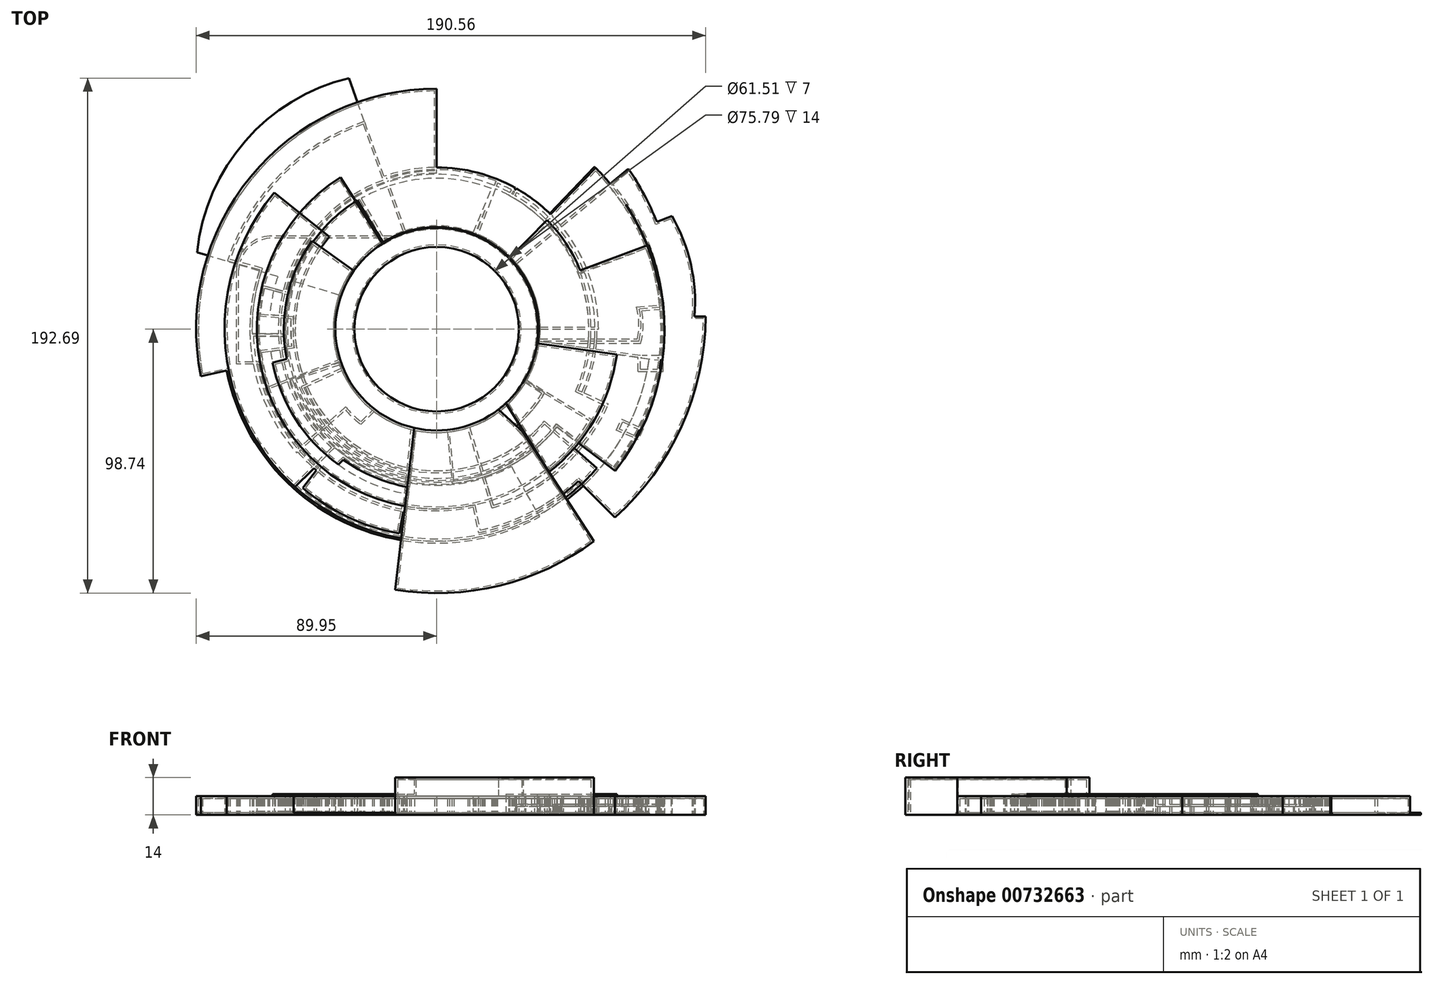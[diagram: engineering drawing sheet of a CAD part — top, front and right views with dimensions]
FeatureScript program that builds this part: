
annotation { "Feature Type Name" : "Feature", "Feature Type Description" : "" }
export const myFeature = defineFeature(function(context is Context, id is Id, definition is map)
    precondition{}
    {
        {
            var Q0;
            Q0=qCreatedBy(makeId("Top.planeOp"),FACE);
            var sketch = newSketch(context, id + "F0", { "sketchPlane" : qUnion([Q0])});
            skCircle(sketch, "E0", {"center": v(0, 0) * mm, "radius": 37.9 * mm});
            skArc(sketch, "E1", {"start": v(-50.12, -59.4) * mm, "mid": v(-33.16, -70.3) * mm, "end": v(-13.98, -76.46) * mm});
            skLineSegment(sketch, "E2", {"start": v(-14.9, 34.84) * mm, "end": v(-60.57, 34.84) * mm});
            skLineSegment(sketch, "E3.bottom", {"start": v(-60.57, 34.84) * mm, "end": v(-14.9, 34.84) * mm});
            skLineSegment(sketch, "E4", {"start": v(28.82, 24.6) * mm, "end": v(71.63, 60.04) * mm});
            skLineSegment(sketch, "E5", {"start": v(-44.15, -51.62) * mm, "end": v(-50.12, -59.4) * mm});
            skLineSegment(sketch, "E6", {"start": v(-66.66, -13.02) * mm, "end": v(-74.87, -13.02) * mm});
            skLineSegment(sketch, "E7", {"start": v(-74.87, -13.02) * mm, "end": v(-74.87, 22.1) * mm});
            skLineSegment(sketch, "E8", {"start": v(-60.57, 34.84) * mm, "end": v(-62.55, 34.84) * mm});
            skArc(sketch, "E9", {"start": v(-60.57, 34.84) * mm, "mid": v(-70.41, 31.5) * mm, "end": v(-74.87, 22.1) * mm});
            skLineSegment(sketch, "E10", {"start": v(53.03, -56.83) * mm, "end": v(66.67, -70.45) * mm});
            skArc(sketch, "E11", {"start": v(66.67, -70.45) * mm, "mid": v(91.53, -36.42) * mm, "end": v(100.6, 4.75) * mm});
            skLineSegment(sketch, "E12", {"start": v(100.6, 4.75) * mm, "end": v(96.37, 4.75) * mm});
            skArc(sketch, "E13", {"start": v(96.37, 4.75) * mm, "mid": v(95.04, 24.16) * mm, "end": v(87.94, 42.28) * mm});
            skLineSegment(sketch, "E14", {"start": v(87.94, 42.28) * mm, "end": v(82.34, 40.14) * mm});
            skArc(sketch, "E15", {"start": v(82.34, 40.14) * mm, "mid": v(77.54, 50.39) * mm, "end": v(71.63, 60.04) * mm});
            skLineSegment(sketch, "E16", {"start": v(-13.98, -76.46) * mm, "end": v(-12.25, -66.8) * mm});
            skLineSegment(sketch, "E17", {"start": v(13.53, -66.56) * mm, "end": v(15.57, -76.15) * mm});
            skArc(sketch, "E18.trimOffspring", {"start": v(15.57, -76.15) * mm, "mid": v(35.63, -69.08) * mm, "end": v(53.03, -56.83) * mm});
            skArc(sketch, "E19.trimOffspring", {"start": v(-12.25, -66.8) * mm, "mid": v(0.65, -67.92) * mm, "end": v(13.53, -66.56) * mm});
            skArc(sketch, "E20.trimOffspring", {"start": v(-66.66, -13.02) * mm, "mid": v(-58.67, -34.22) * mm, "end": v(-44.15, -51.62) * mm});
            skLineSegment(sketch, "E21", {"start": v(68.27, -37.37) * mm, "end": v(69.5, -34.68) * mm});
            skLineSegment(sketch, "E22", {"start": v(69.5, -34.68) * mm, "end": v(76.13, -37.73) * mm});
            skLineSegment(sketch, "E23", {"start": v(76.13, -37.73) * mm, "end": v(74.95, -40.3) * mm});
            skLineSegment(sketch, "E24", {"start": v(74.95, -40.3) * mm, "end": v(68.27, -37.37) * mm});
            skLineSegment(sketch, "E25", {"start": v(76.13, -15) * mm, "end": v(83.94, -15) * mm});
            skLineSegment(sketch, "E26", {"start": v(83.94, -15) * mm, "end": v(83.94, -10.7) * mm});
            skLineSegment(sketch, "E27", {"start": v(83.94, -10.7) * mm, "end": v(76.13, -10.7) * mm});
            skLineSegment(sketch, "E28", {"start": v(76.13, -15) * mm, "end": v(76.13, -10.7) * mm});
            skLineSegment(sketch, "E29", {"start": v(37.63, -4.5) * mm, "end": v(75.65, -4.5) * mm});
            skLineSegment(sketch, "E30", {"start": v(75.7, 7.57) * mm, "end": v(84.16, 8.26) * mm});
            skArc(sketch, "E31", {"start": v(75.65, -4.5) * mm, "mid": v(76.39, 1.54) * mm, "end": v(75.7, 7.57) * mm});
            skArc(sketch, "E32", {"start": v(84.16, 8.26) * mm, "mid": v(78.2, 32.88) * mm, "end": v(64.7, 54.32) * mm});
            skSolve(sketch);
        }
        {
            var Q0;
            {var subQ4=sQuery(id+"F0.wireOp",EDGE,"E29");Q0=makeQuery(id+"F0.imprint","IMPRINT",FACE,{"disambiguationData":[TD([[makeQuery(id+"F0.imprint","IMPRINT",EDGE,{"derivedFrom":subQ4}),1.0]])]});}
            extrude(context, id + "F1", {"entities" : qUnion([Q0]), "depth" : 4 * mm, "offsetDistance" : 25.4 * mm});
        }
        {
            var Q0;
            Q0=makeQuery(id+"F1.opExtrude","CAP_FACE",FACE,{"disambiguationData":[OSD([sQuery(id+"F0.wireOp",EDGE,"E0"),sQuery(id+"F0.wireOp",EDGE,"E4"),sQuery(id+"F0.wireOp",EDGE,"E29"),sQuery(id+"F0.wireOp",EDGE,"E30"),sQuery(id+"F0.wireOp",EDGE,"E31"),sQuery(id+"F0.wireOp",EDGE,"E32")])],"isStart":true});
            shell(context, id + "F2", {"entities" : qUnion([Q0]), "thickness" : 0.8 * mm});
        }
        {
            var Q0;
            Q0=makeQuery(id+"F0.imprint","IMPRINT",FACE,{"disambiguationData":[TD([[makeQuery(id+"F0.imprint","IMPRINT",EDGE,{"derivedFrom":sQuery(id+"F0.wireOp",EDGE,"E1")}),1.0]])]});
            extrude(context, id + "F3", {"entities" : qUnion([Q0]), "operationType" : NewBodyOperationType.ADD, "depth" : 7 * mm, "offsetDistance" : 25.4 * mm});
        }
        {
            var Q0;
            {var subQ0=sQuery(id+"F0.wireOp",EDGE,"E32");var subQ1=sQuery(id+"F0.wireOp",EDGE,"E31");var subQ2=sQuery(id+"F0.wireOp",EDGE,"E30");var subQ3=sQuery(id+"F0.wireOp",EDGE,"E29");var subQ4=sQuery(id+"F0.wireOp",EDGE,"E4");var subQ5=sQuery(id+"F0.wireOp",EDGE,"E0");Q0=makeQuery(id+"F3.boolean.opBoolean","MERGE",FACE,{"derivedFrom":[makeQuery(id+"F1.opExtrude","CAP_FACE",FACE,{"disambiguationData":[OSD([subQ5,subQ4,subQ3,subQ2,subQ1,subQ0])],"isStart":true}),makeQuery(id+"F3.opExtrude","CAP_FACE",FACE,{"disambiguationData":[OSD([subQ5,sQuery(id+"F0.wireOp",EDGE,"E1"),sQuery(id+"F0.wireOp",EDGE,"E3.bottom"),subQ4,sQuery(id+"F0.wireOp",EDGE,"E5"),sQuery(id+"F0.wireOp",EDGE,"E6"),sQuery(id+"F0.wireOp",EDGE,"E7"),sQuery(id+"F0.wireOp",EDGE,"E8"),sQuery(id+"F0.wireOp",EDGE,"E9"),sQuery(id+"F0.wireOp",EDGE,"E10"),sQuery(id+"F0.wireOp",EDGE,"E11"),sQuery(id+"F0.wireOp",EDGE,"E12"),sQuery(id+"F0.wireOp",EDGE,"E13"),sQuery(id+"F0.wireOp",EDGE,"E14"),sQuery(id+"F0.wireOp",EDGE,"E15"),sQuery(id+"F0.wireOp",EDGE,"E16"),sQuery(id+"F0.wireOp",EDGE,"E17"),sQuery(id+"F0.wireOp",EDGE,"E18.trimOffspring"),sQuery(id+"F0.wireOp",EDGE,"E19.trimOffspring"),sQuery(id+"F0.wireOp",EDGE,"E20.trimOffspring"),sQuery(id+"F0.wireOp",EDGE,"E21"),sQuery(id+"F0.wireOp",EDGE,"E22"),sQuery(id+"F0.wireOp",EDGE,"E23"),sQuery(id+"F0.wireOp",EDGE,"E24"),sQuery(id+"F0.wireOp",EDGE,"E25"),sQuery(id+"F0.wireOp",EDGE,"E26"),sQuery(id+"F0.wireOp",EDGE,"E27"),sQuery(id+"F0.wireOp",EDGE,"E28"),subQ3,subQ2,subQ1,subQ0])],"isStart":true})]});}
            shell(context, id + "F4", {"entities" : qUnion([Q0]), "thickness" : 0.8 * mm});
        }
        {
            var Q0;
            Q0=qCreatedBy(makeId("Top.planeOp"),FACE);
            var sketch = newSketch(context, id + "F5", { "sketchPlane" : qUnion([Q0])});
            skArc(sketch, "E33.0", {"start": v(-14.9, 34.84) * mm, "mid": v(-22.7, -30.33) * mm, "end": v(37.63, -4.5) * mm});
            skCircle(sketch, "E34", {"center": v(0, 0) * mm, "radius": 37.9 * mm});
            skCircle(sketch, "E35", {"center": v(0, 0) * mm, "radius": 89.95 * mm});
            skCircle(sketch, "E36", {"center": v(0, 0) * mm, "radius": 80.03 * mm});
            skCircle(sketch, "E37", {"center": v(0, 0) * mm, "radius": 58.4 * mm});
            skLineSegment(sketch, "E38", {"start": v(-88.21, -17.57) * mm, "end": v(-78.51, -15.5) * mm});
            skLineSegment(sketch, "E39", {"start": v(-53.51, -59.5) * mm, "end": v(-38.11, -44.24) * mm});
            skLineSegment(sketch, "E40", {"start": v(27.85, -51.32) * mm, "end": v(17.87, -33.42) * mm});
            skLineSegment(sketch, "E41", {"start": v(17.87, -33.42) * mm, "end": v(38.4, -70.22) * mm});
            skLineSegment(sketch, "E42", {"start": v(0, 37.9) * mm, "end": v(0, 89.95) * mm});
            skSolve(sketch);
        }
        {
            var Q0;
            {var subQ5=sQuery(id+"F5.wireOp",EDGE,"E34");var subQ7=makeQuery(id+"F5.imprint","IMPRINT",VERTEX,{"disambiguationData":[OD(0.0)],"derivedFrom":subQ5});Q0=makeQuery(id+"F5.imprint","IMPRINT",FACE,{"disambiguationData":[TD([[makeQuery(id+"F5.imprint","IMPRINT",EDGE,{"disambiguationData":[TD([[subQ7,1.0]])],"derivedFrom":subQ5}),-1.0]])]});}
            var Q1;
            {var subQ0=sQuery(id+"F5.wireOp",EDGE,"E39");Q1=makeQuery(id+"F5.imprint","IMPRINT",FACE,{"disambiguationData":[TD([[makeQuery(id+"F5.imprint","IMPRINT",EDGE,{"derivedFrom":subQ0}),1.0]])]});}
            var Q2;
            {var subQ0=sQuery(id+"F5.wireOp",EDGE,"E38");Q2=makeQuery(id+"F5.imprint","IMPRINT",FACE,{"disambiguationData":[TD([[makeQuery(id+"F5.imprint","IMPRINT",EDGE,{"derivedFrom":subQ0}),1.0]])]});}
            extrude(context, id + "F6", {"entities" : qUnion([Q0, Q1, Q2]), "depth" : 7 * mm, "offsetDistance" : 25 * mm});
        }
        {
            var Q0;
            Q0=makeQuery(id+"F6.opExtrude","CAP_FACE",FACE,{"disambiguationData":[OSD([sQuery(id+"F5.wireOp",EDGE,"E34"),sQuery(id+"F5.wireOp",EDGE,"E35"),sQuery(id+"F5.wireOp",EDGE,"E36"),sQuery(id+"F5.wireOp",EDGE,"E37"),sQuery(id+"F5.wireOp",EDGE,"E38"),sQuery(id+"F5.wireOp",EDGE,"E39"),sQuery(id+"F5.wireOp",EDGE,"E41"),sQuery(id+"F5.wireOp",EDGE,"E42")])],"isStart":true});
            shell(context, id + "F7", {"entities" : qUnion([Q0]), "thickness" : 0.8 * mm});
        }
        {
            var Q0;
            {var subQ0=sQuery(id+"F5.wireOp",EDGE,"E39");Q0=makeQuery(id+"F5.imprint","IMPRINT",FACE,{"disambiguationData":[TD([[makeQuery(id+"F5.imprint","IMPRINT",EDGE,{"derivedFrom":subQ0}),-1.0]])]});}
            extrude(context, id + "F8", {"entities" : qUnion([Q0]), "operationType" : NewBodyOperationType.ADD, "depth" : 0.8 * mm, "offsetDistance" : 25 * mm});
        }
        {
            var Q0;
            Q0=qCreatedBy(makeId("Top.planeOp"),FACE);
            var sketch = newSketch(context, id + "F9", { "sketchPlane" : qUnion([Q0])});
            skCircle(sketch, "E43.0", {"center": v(0, 0) * mm, "radius": 37.9 * mm});
            skArc(sketch, "E44", {"start": v(-27.02, 77.75) * mm, "mid": v(-58.73, 57.67) * mm, "end": v(-78.23, 25.59) * mm});
            skArc(sketch, "E45", {"start": v(-66.2, 22.28) * mm, "mid": v(-68.46, -13.86) * mm, "end": v(-52.32, -46.28) * mm});
            skArc(sketch, "E46", {"start": v(28.5, 50.2) * mm, "mid": v(5.31, 57.49) * mm, "end": v(-18.81, 54.58) * mm});
            skArc(sketch, "E47", {"start": v(60.48, 0) * mm, "mid": v(52.25, 30.46) * mm, "end": v(29.8, 52.64) * mm});
            skArc(sketch, "E48", {"start": v(-34.1, -30.22) * mm, "mid": v(-31.35, -33.07) * mm, "end": v(-28.35, -35.68) * mm});
            skLineSegment(sketch, "E49", {"start": v(-28.35, -35.68) * mm, "end": v(-22.8, -30.27) * mm});
            skLineSegment(sketch, "E50", {"start": v(-34.1, -30.22) * mm, "end": v(-52.32, -46.28) * mm});
            skLineSegment(sketch, "E51", {"start": v(-66.2, 22.28) * mm, "end": v(-78.23, 25.59) * mm});
            skLineSegment(sketch, "E52", {"start": v(-27.02, 77.75) * mm, "end": v(-18.81, 54.58) * mm});
            skLineSegment(sketch, "E53", {"start": v(28.5, 50.2) * mm, "end": v(29.8, 52.64) * mm});
            skLineSegment(sketch, "E54", {"start": v(60.48, 0) * mm, "end": v(37.9, 0) * mm});
            skSolve(sketch);
        }
        {
            var Q0;
            Q0=makeQuery(id+"F9.imprint","IMPRINT",FACE,{"disambiguationData":[TD([[makeQuery(id+"F9.imprint","IMPRINT",EDGE,{"derivedFrom":sQuery(id+"F9.wireOp",EDGE,"E44")}),1.0]])]});
            extrude(context, id + "F10", {"entities" : qUnion([Q0]), "depth" : 7 * mm, "offsetDistance" : 25 * mm});
        }
        {
            var Q0;
            Q0=makeQuery(id+"F10.opExtrude","CAP_FACE",FACE,{"disambiguationData":[OSD([sQuery(id+"F9.wireOp",EDGE,"E43.0"),sQuery(id+"F9.wireOp",EDGE,"E44"),sQuery(id+"F9.wireOp",EDGE,"E45"),sQuery(id+"F9.wireOp",EDGE,"E46"),sQuery(id+"F9.wireOp",EDGE,"E47"),sQuery(id+"F9.wireOp",EDGE,"E48"),sQuery(id+"F9.wireOp",EDGE,"E49"),sQuery(id+"F9.wireOp",EDGE,"E50"),sQuery(id+"F9.wireOp",EDGE,"E51"),sQuery(id+"F9.wireOp",EDGE,"E52"),sQuery(id+"F9.wireOp",EDGE,"E53"),sQuery(id+"F9.wireOp",EDGE,"E54")])],"isStart":true});
            shell(context, id + "F11", {"entities" : qUnion([Q0]), "thickness" : 0.8 * mm});
        }
        {
            var Q0;
            Q0=qCreatedBy(makeId("Top.planeOp"),FACE);
            var sketch = newSketch(context, id + "F12", { "sketchPlane" : qUnion([Q0])});
            skArc(sketch, "E55", {"start": v(20.63, -66.94) * mm, "mid": v(46.55, -52.34) * mm, "end": v(64.07, -28.31) * mm});
            skArc(sketch, "E56", {"start": v(52.95, -22.88) * mm, "mid": v(54.6, 18.6) * mm, "end": v(27.97, 50.45) * mm});
            skCircle(sketch, "E57.0", {"center": v(0, 0) * mm, "radius": 37.9 * mm});
            skLineSegment(sketch, "E58", {"start": v(11.36, -36.15) * mm, "end": v(20.63, -66.94) * mm});
            skLineSegment(sketch, "E59", {"start": v(52.95, -22.88) * mm, "end": v(64.07, -28.31) * mm});
            skLineSegment(sketch, "E60", {"start": v(27.97, 50.45) * mm, "end": v(29.47, 52.86) * mm});
            skLineSegment(sketch, "E61", {"start": v(-12.23, 35.87) * mm, "end": v(-32.8, 93.95) * mm});
            skLineSegment(sketch, "E62", {"start": v(-35.75, 12.56) * mm, "end": v(-89.55, 28.73) * mm});
            skArc(sketch, "E63", {"start": v(-32.8, 93.95) * mm, "mid": v(-71.59, 70.4) * mm, "end": v(-89.55, 28.73) * mm});
            skArc(sketch, "E64.trimOffspring", {"start": v(29.47, 52.86) * mm, "mid": v(5.3, 60.28) * mm, "end": v(-19.78, 57.2) * mm});
            skSolve(sketch);
        }
        {
            var Q0;
            Q0=makeQuery(id+"F12.imprint","IMPRINT",FACE,{"disambiguationData":[TD([[makeQuery(id+"F12.imprint","IMPRINT",EDGE,{"derivedFrom":sQuery(id+"F12.wireOp",EDGE,"E55")}),1.0]])]});
            extrude(context, id + "F13", {"entities" : qUnion([Q0]), "depth" : 7 * mm, "offsetDistance" : 25 * mm});
        }
        {
            var Q0;
            Q0=makeQuery(id+"F13.opExtrude","CAP_FACE",FACE,{"disambiguationData":[OSD([sQuery(id+"F12.wireOp",EDGE,"E55"),sQuery(id+"F12.wireOp",EDGE,"E56"),sQuery(id+"F12.wireOp",EDGE,"E57.0"),sQuery(id+"F12.wireOp",EDGE,"E58"),sQuery(id+"F12.wireOp",EDGE,"E59"),sQuery(id+"F12.wireOp",EDGE,"E60"),sQuery(id+"F12.wireOp",EDGE,"E61"),sQuery(id+"F12.wireOp",EDGE,"E64.trimOffspring")])],"isStart":true});
            shell(context, id + "F14", {"entities" : qUnion([Q0]), "thickness" : 0.8 * mm});
        }
        {
            var Q0;
            {var subQ0=sQuery(id+"F12.wireOp",EDGE,"E62");Q0=makeQuery(id+"F12.imprint","IMPRINT",FACE,{"disambiguationData":[TD([[makeQuery(id+"F12.imprint","IMPRINT",EDGE,{"derivedFrom":subQ0}),-1.0]])]});}
            extrude(context, id + "F15", {"entities" : qUnion([Q0]), "operationType" : NewBodyOperationType.ADD, "depth" : 0.8 * mm, "offsetDistance" : 25 * mm});
        }
        {
            var Q0;
            Q0=qCreatedBy(makeId("Top.planeOp"),FACE);
            var sketch = newSketch(context, id + "F16", { "sketchPlane" : qUnion([Q0])});
            skCircle(sketch, "E65.0", {"center": v(0, 0) * mm, "radius": 37.9 * mm});
            skArc(sketch, "E66", {"start": v(-50.69, -21.5) * mm, "mid": v(-34.63, -42.8) * mm, "end": v(-10.45, -54.05) * mm});
            skArc(sketch, "E67", {"start": v(-12.18, -68.87) * mm, "mid": v(33.06, -61.63) * mm, "end": v(64.12, -27.94) * mm});
            skArc(sketch, "E68", {"start": v(-15.53, -97.5) * mm, "mid": v(23.44, -95.91) * mm, "end": v(58.75, -79.36) * mm});
            skArc(sketch, "E69", {"start": v(55.06, -23.77) * mm, "mid": v(55.44, 22.88) * mm, "end": v(22.27, 55.69) * mm});
            skLineSegment(sketch, "E70", {"start": v(-50.69, -21.5) * mm, "end": v(-35.05, -14.4) * mm});
            skLineSegment(sketch, "E71", {"start": v(-8.45, -36.94) * mm, "end": v(-15.53, -97.5) * mm});
            skLineSegment(sketch, "E72", {"start": v(58.75, -79.36) * mm, "end": v(32.41, -38.54) * mm});
            skLineSegment(sketch, "E73", {"start": v(32.41, -38.54) * mm, "end": v(23.12, -30.02) * mm});
            skLineSegment(sketch, "E74", {"start": v(55.06, -23.77) * mm, "end": v(64.12, -27.94) * mm});
            skLineSegment(sketch, "E75", {"start": v(22.27, 55.69) * mm, "end": v(14.43, 35.04) * mm});
            skSolve(sketch);
        }
        {
            var Q0;
            {var subQ4=sQuery(id+"F16.wireOp",EDGE,"E66");Q0=makeQuery(id+"F16.imprint","IMPRINT",FACE,{"disambiguationData":[TD([[makeQuery(id+"F16.imprint","IMPRINT",EDGE,{"derivedFrom":subQ4}),1.0]])]});}
            var Q1;
            Q1=makeQuery(id+"F16.imprint","IMPRINT",FACE,{"disambiguationData":[TD([[makeQuery(id+"F16.imprint","IMPRINT",EDGE,{"derivedFrom":sQuery(id+"F16.wireOp",EDGE,"E69")}),1.0]])]});
            extrude(context, id + "F17", {"entities" : qUnion([Q0, Q1]), "depth" : 7 * mm, "offsetDistance" : 25 * mm});
        }
        {
            var Q0;
            {var subQ5=sQuery(id+"F16.wireOp",EDGE,"E68");Q0=makeQuery(id+"F16.imprint","IMPRINT",FACE,{"disambiguationData":[TD([[makeQuery(id+"F16.imprint","IMPRINT",EDGE,{"derivedFrom":subQ5}),1.0]])]});}
            var Q1;
            {var subQ8=sQuery(id+"F16.wireOp",EDGE,"E73");Q1=makeQuery(id+"F16.imprint","IMPRINT",FACE,{"disambiguationData":[TD([[makeQuery(id+"F16.imprint","IMPRINT",EDGE,{"derivedFrom":subQ8}),1.0]])]});}
            extrude(context, id + "F18", {"entities" : qUnion([Q0, Q1]), "depth" : 14 * mm, "offsetDistance" : 25 * mm});
        }
        {
            var Q0;
            Q0=makeQuery(id+"F17.opExtrude","SWEPT_BODY",BODY,{"disambiguationData":[OSD([sQuery(id+"F16.wireOp",EDGE,"E65.0"),sQuery(id+"F16.wireOp",EDGE,"E66"),sQuery(id+"F16.wireOp",EDGE,"E70"),sQuery(id+"F16.wireOp",EDGE,"E71")])]});
            var Q1;
            Q1=makeQuery(id+"F17.opExtrude","SWEPT_BODY",BODY,{"disambiguationData":[OSD([sQuery(id+"F16.wireOp",EDGE,"E65.0"),sQuery(id+"F16.wireOp",EDGE,"E67"),sQuery(id+"F16.wireOp",EDGE,"E69"),sQuery(id+"F16.wireOp",EDGE,"E72"),sQuery(id+"F16.wireOp",EDGE,"E73"),sQuery(id+"F16.wireOp",EDGE,"E74"),sQuery(id+"F16.wireOp",EDGE,"E75")])]});
            var Q2;
            Q2=makeQuery(id+"F18.opExtrude","SWEPT_BODY",BODY,{"disambiguationData":[OSD([sQuery(id+"F16.wireOp",EDGE,"E65.0"),sQuery(id+"F16.wireOp",EDGE,"E68"),sQuery(id+"F16.wireOp",EDGE,"E71"),sQuery(id+"F16.wireOp",EDGE,"E72"),sQuery(id+"F16.wireOp",EDGE,"E73")])]});
            booleanBodies(context, id + "F19", {"operationType" : BooleanOperationType.UNION, "tools" : qUnion([Q0, Q1, Q2])});
        }
        {
            var Q0;
            {var subQ0=sQuery(id+"F16.wireOp",EDGE,"E73");var subQ1=sQuery(id+"F16.wireOp",EDGE,"E72");var subQ2=sQuery(id+"F16.wireOp",EDGE,"E71");var subQ3=sQuery(id+"F16.wireOp",EDGE,"E65.0");Q0=makeQuery(id+"F19.opBoolean","MERGE",FACE,{"derivedFrom":[makeQuery(id+"F17.opExtrude","CAP_FACE",FACE,{"disambiguationData":[OSD([subQ3,sQuery(id+"F16.wireOp",EDGE,"E66"),sQuery(id+"F16.wireOp",EDGE,"E70"),subQ2])],"isStart":true}),makeQuery(id+"F17.opExtrude","CAP_FACE",FACE,{"disambiguationData":[OSD([subQ3,sQuery(id+"F16.wireOp",EDGE,"E67"),sQuery(id+"F16.wireOp",EDGE,"E69"),subQ1,subQ0,sQuery(id+"F16.wireOp",EDGE,"E74"),sQuery(id+"F16.wireOp",EDGE,"E75")])],"isStart":true}),makeQuery(id+"F18.opExtrude","CAP_FACE",FACE,{"disambiguationData":[OSD([subQ3,sQuery(id+"F16.wireOp",EDGE,"E68"),subQ2,subQ1,subQ0])],"isStart":true})]});}
            shell(context, id + "F20", {"entities" : qUnion([Q0]), "thickness" : 0.8 * mm});
        }
        {
            var Q0;
            Q0=qCreatedBy(makeId("Top.planeOp"),FACE);
            var sketch = newSketch(context, id + "F21", { "sketchPlane" : qUnion([Q0])});
            skCircle(sketch, "E76.0", {"center": v(0, 0) * mm, "radius": 37.9 * mm});
            skArc(sketch, "E77", {"start": v(-51.12, 36.15) * mm, "mid": v(-42.94, -45.56) * mm, "end": v(39.11, -48.89) * mm});
            skArc(sketch, "E78", {"start": v(42, -53.51) * mm, "mid": v(58.95, -33.95) * mm, "end": v(67.37, -9.47) * mm});
            skArc(sketch, "E79", {"start": v(-46.7, 33) * mm, "mid": v(-55.94, 11.88) * mm, "end": v(-56.09, -11.18) * mm});
            skArc(sketch, "E80", {"start": v(48.52, -63.93) * mm, "mid": v(69.22, -40.62) * mm, "end": v(79.48, -11.18) * mm});
            skLineSegment(sketch, "E81", {"start": v(-51.12, 36.15) * mm, "end": v(-30.97, 21.83) * mm});
            skLineSegment(sketch, "E82", {"start": v(-11.27, -61.59) * mm, "end": v(-8.19, -37) * mm});
            skLineSegment(sketch, "E83", {"start": v(-61.35, -12.5) * mm, "end": v(-56.09, -11.18) * mm});
            skArc(sketch, "E84", {"start": v(-34.9, -48.86) * mm, "mid": v(-23.49, -55.26) * mm, "end": v(-10.95, -59.04) * mm});
            skLineSegment(sketch, "E85", {"start": v(-34.9, -48.86) * mm, "end": v(-36.78, -50.66) * mm});
            skLineSegment(sketch, "E86", {"start": v(25.85, -27.7) * mm, "end": v(42, -53.51) * mm});
            skLineSegment(sketch, "E87", {"start": v(37.53, -5.26) * mm, "end": v(67.37, -9.47) * mm});
            skLineSegment(sketch, "E88", {"start": v(37.53, -5.26) * mm, "end": v(79.48, -11.18) * mm});
            skLineSegment(sketch, "E89", {"start": v(25.85, -27.7) * mm, "end": v(48.52, -63.93) * mm});
            skSolve(sketch);
        }
        {
            var Q0;
            {var subQ2=sQuery(id+"F21.wireOp",EDGE,"E78");Q0=makeQuery(id+"F21.imprint","IMPRINT",FACE,{"disambiguationData":[TD([[makeQuery(id+"F21.imprint","IMPRINT",EDGE,{"derivedFrom":subQ2}),1.0]])]});}
            var Q1;
            {var subQ1=sQuery(id+"F21.wireOp",EDGE,"E79");Q1=makeQuery(id+"F21.imprint","IMPRINT",FACE,{"disambiguationData":[TD([[makeQuery(id+"F21.imprint","IMPRINT",EDGE,{"derivedFrom":subQ1}),1.0]])]});}
            extrude(context, id + "F22", {"entities" : qUnion([Q0, Q1]), "depth" : 7.8 * mm, "offsetDistance" : 25 * mm});
        }
        {
            var Q0;
            Q0=makeQuery(id+"F22.opExtrude","CAP_FACE",FACE,{"disambiguationData":[OSD([sQuery(id+"F21.wireOp",EDGE,"E76.0"),sQuery(id+"F21.wireOp",EDGE,"E77"),sQuery(id+"F21.wireOp",EDGE,"E79"),sQuery(id+"F21.wireOp",EDGE,"E81"),sQuery(id+"F21.wireOp",EDGE,"E82"),sQuery(id+"F21.wireOp",EDGE,"E83"),sQuery(id+"F21.wireOp",EDGE,"E84"),sQuery(id+"F21.wireOp",EDGE,"E85")])],"isStart":true});
            var Q1;
            Q1=makeQuery(id+"F22.opExtrude","CAP_FACE",FACE,{"disambiguationData":[OSD([sQuery(id+"F21.wireOp",EDGE,"E76.0"),sQuery(id+"F21.wireOp",EDGE,"E78"),sQuery(id+"F21.wireOp",EDGE,"E86"),sQuery(id+"F21.wireOp",EDGE,"E87")])],"isStart":true});
            shell(context, id + "F23", {"entities" : qUnion([Q0, Q1]), "thickness" : 0.8 * mm});
        }
        {
            var Q0;
            {var subQ4=sQuery(id+"F21.wireOp",EDGE,"E79");Q0=makeQuery(id+"F21.imprint","IMPRINT",FACE,{"disambiguationData":[TD([[makeQuery(id+"F21.imprint","IMPRINT",EDGE,{"derivedFrom":subQ4}),-1.0]])]});}
            var Q1;
            Q1=makeQuery(id+"F21.imprint","IMPRINT",FACE,{"disambiguationData":[TD([[makeQuery(id+"F21.imprint","IMPRINT",EDGE,{"derivedFrom":sQuery(id+"F21.wireOp",EDGE,"E78")}),-1.0]])]});
            var Q2;
            {var subQ4=sQuery(id+"F21.wireOp",EDGE,"E84");Q2=makeQuery(id+"F21.imprint","IMPRINT",FACE,{"disambiguationData":[TD([[makeQuery(id+"F21.imprint","IMPRINT",EDGE,{"derivedFrom":subQ4}),-1.0]])]});}
            extrude(context, id + "F24", {"entities" : qUnion([Q0, Q1, Q2]), "depth" : 0.8 * mm, "offsetDistance" : 25 * mm});
        }
        {
            var Q0;
            Q0=qCreatedBy(makeId("Top.planeOp"),FACE);
            var sketch = newSketch(context, id + "F25", { "sketchPlane" : qUnion([Q0])});
            skArc(sketch, "E90", {"start": v(-69.34, -1.77) * mm, "mid": v(-52.5, -45.34) * mm, "end": v(-11.86, -68.35) * mm});
            skArc(sketch, "E91", {"start": v(21.64, 53.01) * mm, "mid": v(-32.67, 47.03) * mm, "end": v(-57.23, -1.77) * mm});
            skLineSegment(sketch, "E92", {"start": v(-57.23, -1.77) * mm, "end": v(-69.34, -1.77) * mm});
            skLineSegment(sketch, "E93", {"start": v(-11.86, -68.35) * mm, "end": v(-8.7, -36.88) * mm});
            skCircle(sketch, "E94.0", {"center": v(0, 0) * mm, "radius": 37.9 * mm});
            skArc(sketch, "E95", {"start": v(-44.2, 43.16) * mm, "mid": v(-57.55, 22.47) * mm, "end": v(-61.75, -1.77) * mm});
            skLineSegment(sketch, "E96", {"start": v(-44.2, 43.16) * mm, "end": v(-41.1, 39.88) * mm});
            skLineSegment(sketch, "E97", {"start": v(14.07, 35.19) * mm, "end": v(21.64, 53.01) * mm});
            skSolve(sketch);
        }
        {
            var Q0;
            {var subQ6=sQuery(id+"F25.wireOp",EDGE,"E90");Q0=makeQuery(id+"F25.imprint","IMPRINT",FACE,{"disambiguationData":[TD([[makeQuery(id+"F25.imprint","IMPRINT",EDGE,{"derivedFrom":subQ6}),1.0]])]});}
            extrude(context, id + "F26", {"entities" : qUnion([Q0]), "depth" : 7 * mm, "offsetDistance" : 25 * mm});
        }
        {
            var Q0;
            Q0=makeQuery(id+"F26.opExtrude","CAP_FACE",FACE,{"disambiguationData":[OSD([sQuery(id+"F25.wireOp",EDGE,"E90"),sQuery(id+"F25.wireOp",EDGE,"E91"),sQuery(id+"F25.wireOp",EDGE,"E92"),sQuery(id+"F25.wireOp",EDGE,"E93"),sQuery(id+"F25.wireOp",EDGE,"E94.0"),sQuery(id+"F25.wireOp",EDGE,"E97")])],"isStart":true});
            shell(context, id + "F27", {"entities" : qUnion([Q0]), "thickness" : 0.8 * mm});
        }
        {
            var Q0;
            {var subQ4=sQuery(id+"F25.wireOp",EDGE,"E95");Q0=makeQuery(id+"F25.imprint","IMPRINT",FACE,{"disambiguationData":[TD([[makeQuery(id+"F25.imprint","IMPRINT",EDGE,{"derivedFrom":subQ4}),1.0]])]});}
            extrude(context, id + "F28", {"entities" : qUnion([Q0]), "operationType" : NewBodyOperationType.ADD, "depth" : 0.8 * mm, "offsetDistance" : 25 * mm});
        }
        {
            var Q0;
            Q0=qCreatedBy(makeId("Top.planeOp"),FACE);
            var sketch = newSketch(context, id + "F29", { "sketchPlane" : qUnion([Q0])});
            skCircle(sketch, "E98.0", {"center": v(0, 0) * mm, "radius": 37.9 * mm});
            skArc(sketch, "E99", {"start": v(83.87, -11.69) * mm, "mid": v(80.19, 27.23) * mm, "end": v(59.41, 60.35) * mm});
            skArc(sketch, "E100", {"start": v(-54.52, 3.94) * mm, "mid": v(-54.65, -1.23) * mm, "end": v(-54.29, -6.38) * mm});
            skLineSegment(sketch, "E101", {"start": v(-66.8, 4.88) * mm, "end": v(-54.52, 3.94) * mm});
            skLineSegment(sketch, "E102", {"start": v(-54.52, 3.94) * mm, "end": v(-54.29, -6.38) * mm});
            skLineSegment(sketch, "E103", {"start": v(-54.29, -6.38) * mm, "end": v(-66.48, -8.13) * mm});
            skLineSegment(sketch, "E104", {"start": v(-63.1, -22.46) * mm, "end": v(-35.93, -12.05) * mm});
            skLineSegment(sketch, "E105", {"start": v(37.54, -5.2) * mm, "end": v(83.87, -11.69) * mm});
            skLineSegment(sketch, "E106", {"start": v(59.41, 60.35) * mm, "end": v(40.8, 41.17) * mm});
            skArc(sketch, "E107", {"start": v(40.8, 41.17) * mm, "mid": v(-15.66, 55.8) * mm, "end": v(-56.27, 13.92) * mm});
            skLineSegment(sketch, "E108", {"start": v(-44.22, 42.71) * mm, "end": v(-41.67, 40.29) * mm});
            skArc(sketch, "E109.trimOffspring", {"start": v(-44.22, 42.71) * mm, "mid": v(-53.78, 29.8) * mm, "end": v(-59.66, 14.85) * mm});
            skLineSegment(sketch, "E110", {"start": v(-56.27, 13.92) * mm, "end": v(-64.96, 16.29) * mm});
            skArc(sketch, "E111.trimOffspring", {"start": v(-64.96, 16.29) * mm, "mid": v(-66.9, -3.22) * mm, "end": v(-63.1, -22.46) * mm});
            skSolve(sketch);
        }
        {
            var Q0;
            Q0=makeQuery(id+"F29.imprint","IMPRINT",FACE,{"disambiguationData":[TD([[makeQuery(id+"F29.imprint","IMPRINT",EDGE,{"derivedFrom":sQuery(id+"F29.wireOp",EDGE,"E99")}),1.0]])]});
            extrude(context, id + "F30", {"entities" : qUnion([Q0]), "depth" : 7 * mm, "offsetDistance" : 25 * mm});
        }
        {
            var Q0;
            Q0=makeQuery(id+"F30.opExtrude","CAP_FACE",FACE,{"disambiguationData":[OSD([sQuery(id+"F29.wireOp",EDGE,"E98.0"),sQuery(id+"F29.wireOp",EDGE,"E99"),sQuery(id+"F29.wireOp",EDGE,"E101"),sQuery(id+"F29.wireOp",EDGE,"E102"),sQuery(id+"F29.wireOp",EDGE,"E103"),sQuery(id+"F29.wireOp",EDGE,"E104"),sQuery(id+"F29.wireOp",EDGE,"E105"),sQuery(id+"F29.wireOp",EDGE,"E106"),sQuery(id+"F29.wireOp",EDGE,"E107"),sQuery(id+"F29.wireOp",EDGE,"E110"),sQuery(id+"F29.wireOp",EDGE,"E111.trimOffspring")])],"isStart":true});
            shell(context, id + "F31", {"entities" : qUnion([Q0]), "thickness" : 0.8 * mm});
        }
        {
            var Q0;
            {var subQ3=sQuery(id+"F29.wireOp",EDGE,"E108");Q0=makeQuery(id+"F29.imprint","IMPRINT",FACE,{"disambiguationData":[TD([[makeQuery(id+"F29.imprint","IMPRINT",EDGE,{"derivedFrom":subQ3}),-1.0]])]});}
            var Q1;
            Q1=makeQuery(id+"F29.imprint","IMPRINT",FACE,{"disambiguationData":[TD([[makeQuery(id+"F29.imprint","IMPRINT",EDGE,{"derivedFrom":sQuery(id+"F29.wireOp",EDGE,"E100")}),-1.0]])]});
            extrude(context, id + "F32", {"entities" : qUnion([Q0, Q1]), "operationType" : NewBodyOperationType.ADD, "depth" : 0.8 * mm, "offsetDistance" : 25 * mm});
        }
        {
            var Q0;
            Q0=qCreatedBy(makeId("Top.planeOp"),FACE);
            var sketch = newSketch(context, id + "F33", { "sketchPlane" : qUnion([Q0])});
            skCircle(sketch, "E112.0", {"center": v(0, 0) * mm, "radius": 37.9 * mm});
            skCircle(sketch, "E113", {"center": v(0, 0) * mm, "radius": 84.67 * mm});
            skArc(sketch, "E114", {"start": v(5.74, -57.65) * mm, "mid": v(27.46, -51.02) * mm, "end": v(44.95, -36.55) * mm});
            skArc(sketch, "E115", {"start": v(41.7, 42.6) * mm, "mid": v(7.12, 59.2) * mm, "end": v(-30.41, 51.28) * mm});
            skLineSegment(sketch, "E116", {"start": v(-19.72, 32.36) * mm, "end": v(-30.41, 51.28) * mm});
            skLineSegment(sketch, "E117", {"start": v(5.74, -57.65) * mm, "end": v(3.94, -37.69) * mm});
            skLineSegment(sketch, "E118", {"start": v(44.95, -36.55) * mm, "end": v(66.27, -52.7) * mm});
            skLineSegment(sketch, "E119", {"start": v(53.77, 21.58) * mm, "end": v(78.7, 31.24) * mm});
            skLineSegment(sketch, "E120", {"start": v(41.7, 42.6) * mm, "end": v(58.97, 60.76) * mm});
            skArc(sketch, "E121.trimOffspring", {"start": v(53.77, 21.58) * mm, "mid": v(18.59, 54.87) * mm, "end": v(-29.58, 49.81) * mm});
            skSolve(sketch);
        }
        {
            var Q0;
            Q0=makeQuery(id+"F33.imprint","IMPRINT",FACE,{"disambiguationData":[TD([[makeQuery(id+"F33.imprint","IMPRINT",EDGE,{"derivedFrom":sQuery(id+"F33.wireOp",EDGE,"E114")}),1.0]])]});
            extrude(context, id + "F34", {"entities" : qUnion([Q0]), "depth" : 7 * mm, "offsetDistance" : 25 * mm});
        }
        {
            var Q0;
            Q0=makeQuery(id+"F34.opExtrude","CAP_FACE",FACE,{"disambiguationData":[OSD([sQuery(id+"F33.wireOp",EDGE,"E112.0"),sQuery(id+"F33.wireOp",EDGE,"E113"),sQuery(id+"F33.wireOp",EDGE,"E114"),sQuery(id+"F33.wireOp",EDGE,"E116"),sQuery(id+"F33.wireOp",EDGE,"E117"),sQuery(id+"F33.wireOp",EDGE,"E118"),sQuery(id+"F33.wireOp",EDGE,"E119"),sQuery(id+"F33.wireOp",EDGE,"E121.trimOffspring")])],"isStart":true});
            shell(context, id + "F35", {"entities" : qUnion([Q0]), "thickness" : 0.8 * mm});
        }
        {
            var Q0;
            {var subQ1=sQuery(id+"F33.wireOp",EDGE,"E115");Q0=makeQuery(id+"F33.imprint","IMPRINT",FACE,{"disambiguationData":[TD([[makeQuery(id+"F33.imprint","IMPRINT",EDGE,{"derivedFrom":subQ1}),1.0]])]});}
            extrude(context, id + "F36", {"entities" : qUnion([Q0]), "operationType" : NewBodyOperationType.ADD, "depth" : 0.8 * mm, "offsetDistance" : 25 * mm});
        }
        {
            var Q0;
            Q0=qCreatedBy(makeId("Top.planeOp"),FACE);
            var sketch = newSketch(context, id + "F37", { "sketchPlane" : qUnion([Q0])});
            skCircle(sketch, "E122.0", {"center": v(0, 0) * mm, "radius": 37.9 * mm});
            skCircle(sketch, "E123", {"center": v(0, 0) * mm, "radius": 58.02 * mm});
            skCircle(sketch, "E124", {"center": v(0, 0) * mm, "radius": 85.2 * mm});
            skLineSegment(sketch, "E125", {"start": v(-35.82, -12.37) * mm, "end": v(-54.89, -18.8) * mm});
            skLineSegment(sketch, "E126", {"start": v(27.15, 26.43) * mm, "end": v(41.28, 40.77) * mm});
            skLineSegment(sketch, "E127", {"start": v(53.67, 22.04) * mm, "end": v(79.16, 31.53) * mm});
            skLineSegment(sketch, "E128", {"start": v(45, -36.63) * mm, "end": v(66.73, -52.99) * mm});
            skSolve(sketch);
        }
        {
            var Q0;
            {var subQ0=sQuery(id+"F37.wireOp",EDGE,"E127");Q0=makeQuery(id+"F37.imprint","IMPRINT",FACE,{"disambiguationData":[TD([[makeQuery(id+"F37.imprint","IMPRINT",EDGE,{"derivedFrom":subQ0}),-1.0]])]});}
            var Q1;
            {var subQ3=sQuery(id+"F37.wireOp",EDGE,"E125");Q1=makeQuery(id+"F37.imprint","IMPRINT",FACE,{"disambiguationData":[TD([[makeQuery(id+"F37.imprint","IMPRINT",EDGE,{"derivedFrom":subQ3}),1.0]])]});}
            extrude(context, id + "F38", {"entities" : qUnion([Q0, Q1]), "depth" : 7 * mm, "offsetDistance" : 25 * mm});
        }
        {
            var Q0;
            Q0=qCreatedBy(makeId("Top.planeOp"),FACE);
            var sketch = newSketch(context, id + "F39", { "sketchPlane" : qUnion([Q0])});
            skArc(sketch, "E129.0", {"start": v(-19.95, 32.22) * mm, "mid": v(-26.33, -27.25) * mm, "end": v(32.88, -18.83) * mm});
            skArc(sketch, "E130", {"start": v(-29.65, 48.23) * mm, "mid": v(-45.87, -33.2) * mm, "end": v(36.54, -43.25) * mm});
            skArc(sketch, "E131", {"start": v(-24.6, 39.9) * mm, "mid": v(-32.8, -33.47) * mm, "end": v(40.38, -23.8) * mm});
            skLineSegment(sketch, "E132", {"start": v(-29.65, 48.23) * mm, "end": v(-19.95, 32.22) * mm});
            skLineSegment(sketch, "E133", {"start": v(36.54, -43.25) * mm, "end": v(29.73, -36.24) * mm});
            skLineSegment(sketch, "E134", {"start": v(40.38, -23.8) * mm, "end": v(32.88, -18.83) * mm});
            skSolve(sketch);
        }
        {
            var Q0;
            Q0 = qSketchRegion(id + "F39", true);
            extrude(context, id + "F40", {"entities" : qUnion([Q0]), "depth" : 7 * mm, "offsetDistance" : 25 * mm});
        }
        {
            var Q0;
            Q0=qCreatedBy(makeId("Top.planeOp"),FACE);
            var sketch = newSketch(context, id + "F41", { "sketchPlane" : qUnion([Q0])});
            skCircle(sketch, "E135", {"center": v(0, 0) * mm, "radius": 30.75 * mm});
            skCircle(sketch, "E136", {"center": v(0, 0) * mm, "radius": 38.2 * mm});
            skCircle(sketch, "E137", {"center": v(0, 0) * mm, "radius": 67.27 * mm});
            skLineSegment(sketch, "E138", {"start": v(-36, 56.82) * mm, "end": v(-20.39, 32.31) * mm});
            skLineSegment(sketch, "E139", {"start": v(33.26, -18.8) * mm, "end": v(58.1, -33.9) * mm});
            skSolve(sketch);
        }
        {
            var Q0;
            {var subQ0=sQuery(id+"F41.wireOp",EDGE,"E138");Q0=makeQuery(id+"F41.imprint","IMPRINT",FACE,{"disambiguationData":[TD([[makeQuery(id+"F41.imprint","IMPRINT",EDGE,{"derivedFrom":subQ0}),-1.0]])]});}
            var Q1;
            Q1=makeQuery(id+"F41.imprint","IMPRINT",FACE,{"disambiguationData":[TD([[makeQuery(id+"F41.imprint","IMPRINT",EDGE,{"derivedFrom":sQuery(id+"F41.wireOp",EDGE,"E135")}),-1.0]])]});
            extrude(context, id + "F42", {"entities" : qUnion([Q0, Q1]), "depth" : 7 * mm, "offsetDistance" : 25 * mm});
        }
        {
            var Q0;
            Q0=qCreatedBy(makeId("Top.planeOp"),FACE);
            var sketch = newSketch(context, id + "F43", { "sketchPlane" : qUnion([Q0])});
            skArc(sketch, "E140", {"start": v(-40.14, 34.54) * mm, "mid": v(-34.47, -40.2) * mm, "end": v(40.26, -34.4) * mm});
            skArc(sketch, "E141", {"start": v(-60.71, 51.04) * mm, "mid": v(-51.54, -60.29) * mm, "end": v(59.86, -52.03) * mm});
            skLineSegment(sketch, "E142", {"start": v(-40.14, 34.54) * mm, "end": v(-60.71, 51.04) * mm});
            skLineSegment(sketch, "E143", {"start": v(40.26, -34.4) * mm, "end": v(59.86, -52.03) * mm});
            skSolve(sketch);
        }
        {
            var Q0;
            Q0 = qSketchRegion(id + "F43", true);
            extrude(context, id + "F44", {"entities" : qUnion([Q0]), "depth" : 7 * mm, "offsetDistance" : 25 * mm});
        }
        {
            var Q0;
            Q0=makeQuery(id+"F44.opExtrude","CAP_FACE",FACE,{"disambiguationData":[OSD([sQuery(id+"F43.wireOp",EDGE,"E140"),sQuery(id+"F43.wireOp",EDGE,"E141"),sQuery(id+"F43.wireOp",EDGE,"E142"),sQuery(id+"F43.wireOp",EDGE,"E143")])],"isStart":true});
            shell(context, id + "F45", {"entities" : qUnion([Q0]), "thickness" : 0.8 * mm});
        }
        {
            var Q0;
            Q0=makeQuery(id+"F42.opExtrude","CAP_FACE",FACE,{"disambiguationData":[OSD([sQuery(id+"F41.wireOp",EDGE,"E135"),sQuery(id+"F41.wireOp",EDGE,"E136"),sQuery(id+"F41.wireOp",EDGE,"E137"),sQuery(id+"F41.wireOp",EDGE,"E138"),sQuery(id+"F41.wireOp",EDGE,"E139")])],"isStart":true});
            shell(context, id + "F46", {"entities" : qUnion([Q0]), "thickness" : 0.8 * mm});
        }
        {
            var Q0;
            Q0=makeQuery(id+"F40.opExtrude","CAP_FACE",FACE,{"disambiguationData":[OSD([sQuery(id+"F39.wireOp",EDGE,"E129.0"),sQuery(id+"F39.wireOp",EDGE,"E130"),sQuery(id+"F39.wireOp",EDGE,"E131"),sQuery(id+"F39.wireOp",EDGE,"E132"),sQuery(id+"F39.wireOp",EDGE,"E133"),sQuery(id+"F39.wireOp",EDGE,"E134")])],"isStart":true});
            shell(context, id + "F47", {"entities" : qUnion([Q0]), "thickness" : 0.8 * mm});
        }
        {
            var Q0;
            Q0=makeQuery(id+"F38.opExtrude","CAP_FACE",FACE,{"disambiguationData":[OSD([sQuery(id+"F37.wireOp",EDGE,"E122.0"),sQuery(id+"F37.wireOp",EDGE,"E123"),sQuery(id+"F37.wireOp",EDGE,"E124"),sQuery(id+"F37.wireOp",EDGE,"E125"),sQuery(id+"F37.wireOp",EDGE,"E126"),sQuery(id+"F37.wireOp",EDGE,"E127"),sQuery(id+"F37.wireOp",EDGE,"E128")])],"isStart":true});
            shell(context, id + "F48", {"entities" : qUnion([Q0]), "thickness" : 0.8 * mm});
        }
    });
